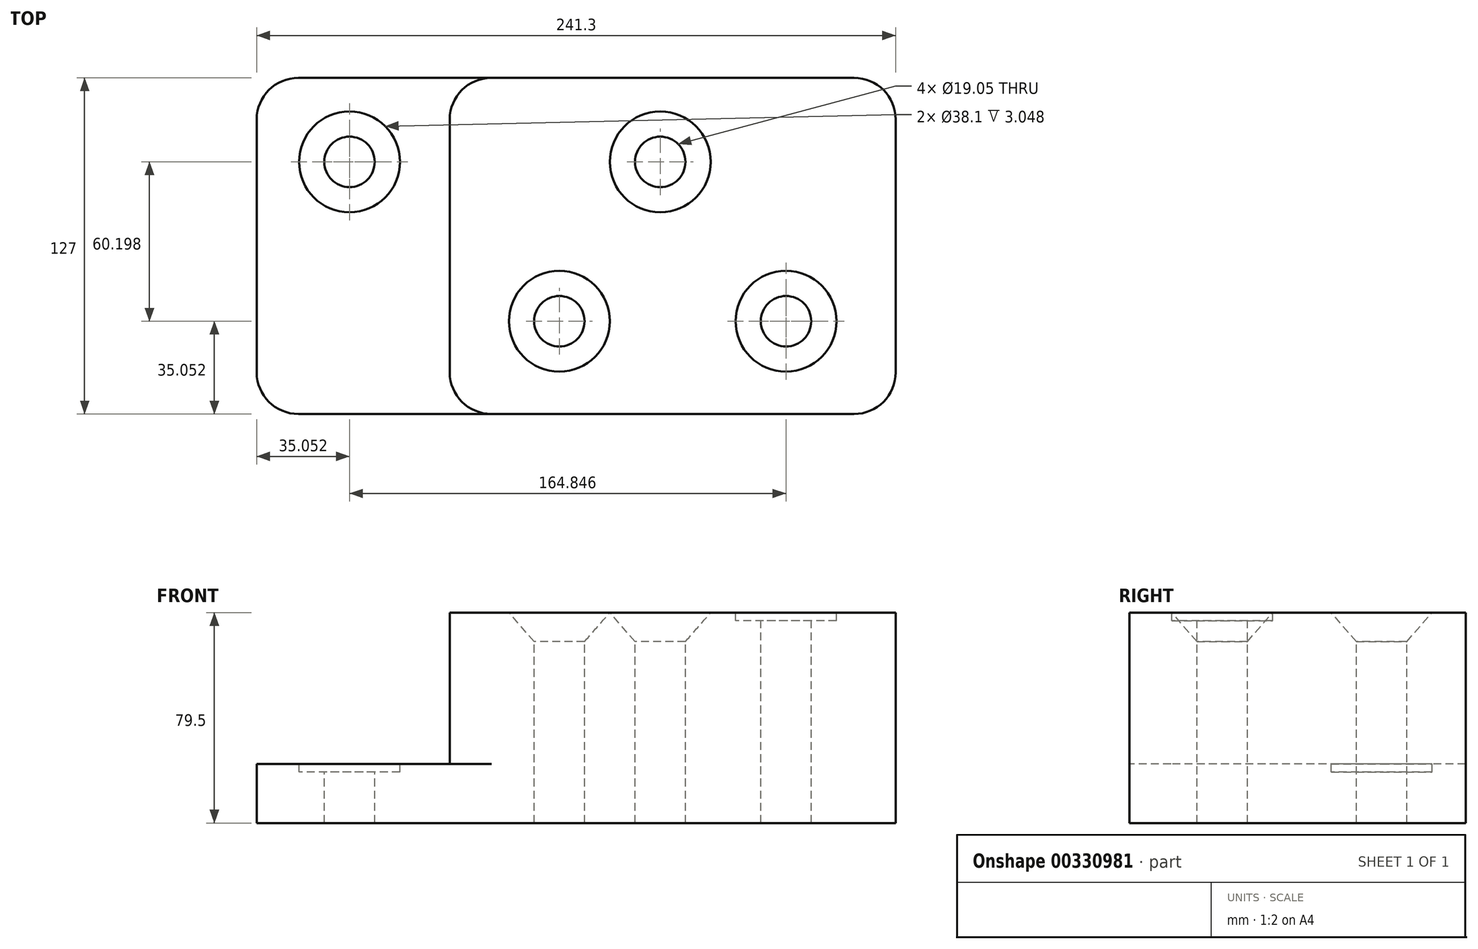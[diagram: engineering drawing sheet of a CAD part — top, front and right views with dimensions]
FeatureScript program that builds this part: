
annotation { "Feature Type Name" : "Feature", "Feature Type Description" : "" }
export const myFeature = defineFeature(function(context is Context, id is Id, definition is map)
    precondition{}
    {
        {
            var Q0;
            Q0=qCreatedBy(makeId("Top.planeOp"),FACE);
            var sketch = newSketch(context, id + "F0", { "sketchPlane" : qUnion([Q0])});
            skLineSegment(sketch, "E0", {"start": v(88.65, 0) * mm, "end": v(225.55, 0) * mm});
            skLineSegment(sketch, "E1", {"start": v(241.3, 15.75) * mm, "end": v(241.3, 111.25) * mm});
            skLineSegment(sketch, "E2", {"start": v(225.55, 127) * mm, "end": v(88.65, 127) * mm});
            skLineSegment(sketch, "E3", {"start": v(0, 111.25) * mm, "end": v(0, 15.75) * mm});
            skLineSegment(sketch, "E4", {"start": v(72.9, 111.25) * mm, "end": v(72.9, 15.75) * mm});
            skPoint(sketch, "E5.visualSharp", {"position": v(241.3, 127) * mm});
            skArc(sketch, "E5.filletArc", {"start": v(241.3, 111.25) * mm, "mid": v(236.69, 122.39) * mm, "end": v(225.55, 127) * mm});
            skPoint(sketch, "E6.visualSharp", {"position": v(241.3, 0) * mm});
            skArc(sketch, "E6.filletArc", {"start": v(225.55, 0) * mm, "mid": v(236.69, 4.61) * mm, "end": v(241.3, 15.75) * mm});
            skPoint(sketch, "E7.visualSharp", {"position": v(0, 0) * mm});
            skArc(sketch, "E7.filletArc", {"start": v(0, 15.75) * mm, "mid": v(4.61, 4.61) * mm, "end": v(15.75, 0) * mm});
            skPoint(sketch, "E8.visualSharp", {"position": v(0, 127) * mm});
            skArc(sketch, "E8.filletArc", {"start": v(15.75, 127) * mm, "mid": v(4.61, 122.39) * mm, "end": v(0, 111.25) * mm});
            skArc(sketch, "E9.filletArc", {"start": v(88.65, 127) * mm, "mid": v(77.51, 122.39) * mm, "end": v(72.9, 111.25) * mm});
            skArc(sketch, "E10.filletArc", {"start": v(72.9, 15.75) * mm, "mid": v(77.51, 4.61) * mm, "end": v(88.65, 0) * mm});
            skLineSegment(sketch, "E11", {"start": v(88.65, 127) * mm, "end": v(15.75, 127) * mm});
            skLineSegment(sketch, "E12", {"start": v(88.65, 0) * mm, "end": v(15.75, 0) * mm});
            skLineSegment(sketch, "E13", {"start": v(152.4, 127) * mm, "end": v(152.4, 95.25) * mm, "construction": true});
            skLineSegment(sketch, "E14", {"start": v(152.4, 95.25) * mm, "end": v(241.3, 95.25) * mm, "construction": true});
            skLineSegment(sketch, "E15", {"start": v(241.3, 35.05) * mm, "end": v(114.3, 35.05) * mm, "construction": true});
            skLineSegment(sketch, "E16", {"start": v(114.3, 35.05) * mm, "end": v(114.3, 127) * mm, "construction": true});
            skLineSegment(sketch, "E17", {"start": v(35.05, 127) * mm, "end": v(35.05, 95.25) * mm, "construction": true});
            skLineSegment(sketch, "E18", {"start": v(35.05, 95.25) * mm, "end": v(0, 95.25) * mm, "construction": true});
            skLineSegment(sketch, "E19", {"start": v(199.9, 35.05) * mm, "end": v(199.9, 127) * mm, "construction": true});
            skSolve(sketch);
        }
        {
            var Q0;
            Q0=makeQuery(id+"F0.imprint","IMPRINT",FACE,{"disambiguationData":[TD([[makeQuery(id+"F0.imprint","IMPRINT",EDGE,{"derivedFrom":sQuery(id+"F0.wireOp",EDGE,"E3")}),1.0]])]});
            extrude(context, id + "F1", {"entities" : qUnion([Q0]), "depth" : 22.35 * mm});
        }
        {
            var Q0;
            Q0=makeQuery(id+"F0.imprint","IMPRINT",FACE,{"disambiguationData":[TD([[makeQuery(id+"F0.imprint","IMPRINT",EDGE,{"derivedFrom":sQuery(id+"F0.wireOp",EDGE,"E1")}),1.0]])]});
            extrude(context, id + "F2", {"entities" : qUnion([Q0]), "operationType" : NewBodyOperationType.ADD, "depth" : 79.5 * mm});
        }
        {
            var Q0;
            Q0=makeQuery(id+"F2.opExtrude","CAP_FACE",FACE,{"disambiguationData":[OSD([sQuery(id+"F0.wireOp",EDGE,"E0"),sQuery(id+"F0.wireOp",EDGE,"E1"),sQuery(id+"F0.wireOp",EDGE,"E2"),sQuery(id+"F0.wireOp",EDGE,"E4"),sQuery(id+"F0.wireOp",EDGE,"E5.filletArc"),sQuery(id+"F0.wireOp",EDGE,"E6.filletArc"),sQuery(id+"F0.wireOp",EDGE,"E9.filletArc"),sQuery(id+"F0.wireOp",EDGE,"E10.filletArc")])],"isStart":false});
            var sketch = newSketch(context, id + "F3", { "sketchPlane" : qUnion([Q0])});
            skPoint(sketch, "E20.0", {"position": v(35.05, 95.25) * mm});
            skPoint(sketch, "E21.0", {"position": v(152.4, 95.25) * mm});
            skPoint(sketch, "E22.0", {"position": v(114.3, 35.05) * mm});
            skPoint(sketch, "E23.0", {"position": v(199.9, 35.05) * mm});
            skSolve(sketch);
        }
        {
            var Q0;
            Q0=sQuery(id+"F3.wireOp",VERTEX,"E23.0");
            var Q1;
            Q1=makeQuery(id+"F1.opExtrude","SWEPT_BODY",BODY,{"disambiguationData":[OSD([sQuery(id+"F0.wireOp",EDGE,"E3"),sQuery(id+"F0.wireOp",EDGE,"E4"),sQuery(id+"F0.wireOp",EDGE,"E7.filletArc"),sQuery(id+"F0.wireOp",EDGE,"E8.filletArc"),sQuery(id+"F0.wireOp",EDGE,"E9.filletArc"),sQuery(id+"F0.wireOp",EDGE,"E10.filletArc"),sQuery(id+"F0.wireOp",EDGE,"E11"),sQuery(id+"F0.wireOp",EDGE,"E12")])]});
            hole(context, id + "F4", {"style" : HoleStyle.C_BORE, "endStyle" : HoleEndStyle.BLIND, "holeDiameter" : 19.05 * mm, "cBoreDiameter" : 38.1 * mm, "cBoreDepth" : 3.05 * mm, "holeDepth" : 79.5 * mm, "tappedDepth" : 12.7 * mm, "tapClearance" : 3, "startFromSketch" : true, "locations" : qUnion([Q0]), "scope" : qUnion([Q1])});
        }
        {
            var Q0;
            Q0=makeQuery(id+"F1.opExtrude","CAP_FACE",FACE,{"disambiguationData":[OSD([sQuery(id+"F0.wireOp",EDGE,"E3"),sQuery(id+"F0.wireOp",EDGE,"E4"),sQuery(id+"F0.wireOp",EDGE,"E7.filletArc"),sQuery(id+"F0.wireOp",EDGE,"E8.filletArc"),sQuery(id+"F0.wireOp",EDGE,"E9.filletArc"),sQuery(id+"F0.wireOp",EDGE,"E10.filletArc"),sQuery(id+"F0.wireOp",EDGE,"E11"),sQuery(id+"F0.wireOp",EDGE,"E12")])],"isStart":false});
            var sketch = newSketch(context, id + "F5", { "sketchPlane" : qUnion([Q0])});
            skPoint(sketch, "E24.0", {"position": v(35.05, 95.25) * mm});
            skSolve(sketch);
        }
        {
            var Q0;
            Q0=sQuery(id+"F5.wireOp",VERTEX,"E24.0");
            var Q1;
            Q1=makeQuery(id+"F1.opExtrude","SWEPT_BODY",BODY,{"disambiguationData":[OSD([sQuery(id+"F0.wireOp",EDGE,"E3"),sQuery(id+"F0.wireOp",EDGE,"E4"),sQuery(id+"F0.wireOp",EDGE,"E7.filletArc"),sQuery(id+"F0.wireOp",EDGE,"E8.filletArc"),sQuery(id+"F0.wireOp",EDGE,"E9.filletArc"),sQuery(id+"F0.wireOp",EDGE,"E10.filletArc"),sQuery(id+"F0.wireOp",EDGE,"E11"),sQuery(id+"F0.wireOp",EDGE,"E12")])]});
            hole(context, id + "F6", {"style" : HoleStyle.C_BORE, "endStyle" : HoleEndStyle.BLIND, "holeDiameter" : 19.05 * mm, "cBoreDiameter" : 38.1 * mm, "cBoreDepth" : 3.05 * mm, "holeDepth" : 79.5 * mm, "tappedDepth" : 12.7 * mm, "tapClearance" : 3, "startFromSketch" : true, "locations" : qUnion([Q0]), "scope" : qUnion([Q1])});
        }
        {
            var Q0;
            Q0=makeQuery(id+"F2.opExtrude","CAP_FACE",FACE,{"disambiguationData":[OSD([sQuery(id+"F0.wireOp",EDGE,"E0"),sQuery(id+"F0.wireOp",EDGE,"E1"),sQuery(id+"F0.wireOp",EDGE,"E2"),sQuery(id+"F0.wireOp",EDGE,"E4"),sQuery(id+"F0.wireOp",EDGE,"E5.filletArc"),sQuery(id+"F0.wireOp",EDGE,"E6.filletArc"),sQuery(id+"F0.wireOp",EDGE,"E9.filletArc"),sQuery(id+"F0.wireOp",EDGE,"E10.filletArc")])],"isStart":false});
            var sketch = newSketch(context, id + "F7", { "sketchPlane" : qUnion([Q0])});
            skPoint(sketch, "E25.0", {"position": v(152.4, 95.25) * mm});
            skPoint(sketch, "E26.0", {"position": v(114.3, 35.05) * mm});
            skSolve(sketch);
        }
        {
            var Q0;
            Q0=sQuery(id+"F7.wireOp",VERTEX,"E25.0");
            var Q1;
            Q1=sQuery(id+"F7.wireOp",VERTEX,"E26.0");
            var Q2;
            Q2=makeQuery(id+"F1.opExtrude","SWEPT_BODY",BODY,{"disambiguationData":[OSD([sQuery(id+"F0.wireOp",EDGE,"E3"),sQuery(id+"F0.wireOp",EDGE,"E4"),sQuery(id+"F0.wireOp",EDGE,"E7.filletArc"),sQuery(id+"F0.wireOp",EDGE,"E8.filletArc"),sQuery(id+"F0.wireOp",EDGE,"E9.filletArc"),sQuery(id+"F0.wireOp",EDGE,"E10.filletArc"),sQuery(id+"F0.wireOp",EDGE,"E11"),sQuery(id+"F0.wireOp",EDGE,"E12")])]});
            hole(context, id + "F8", {"style" : HoleStyle.C_SINK, "endStyle" : HoleEndStyle.BLIND, "holeDiameter" : 19.05 * mm, "cSinkDiameter" : 38.1 * mm, "cSinkAngle" : 82 * degree, "holeDepth" : 79.5 * mm, "tappedDepth" : 12.7 * mm, "tapClearance" : 3, "startFromSketch" : true, "locations" : qUnion([Q0, Q1]), "scope" : qUnion([Q2])});
        }
    });
